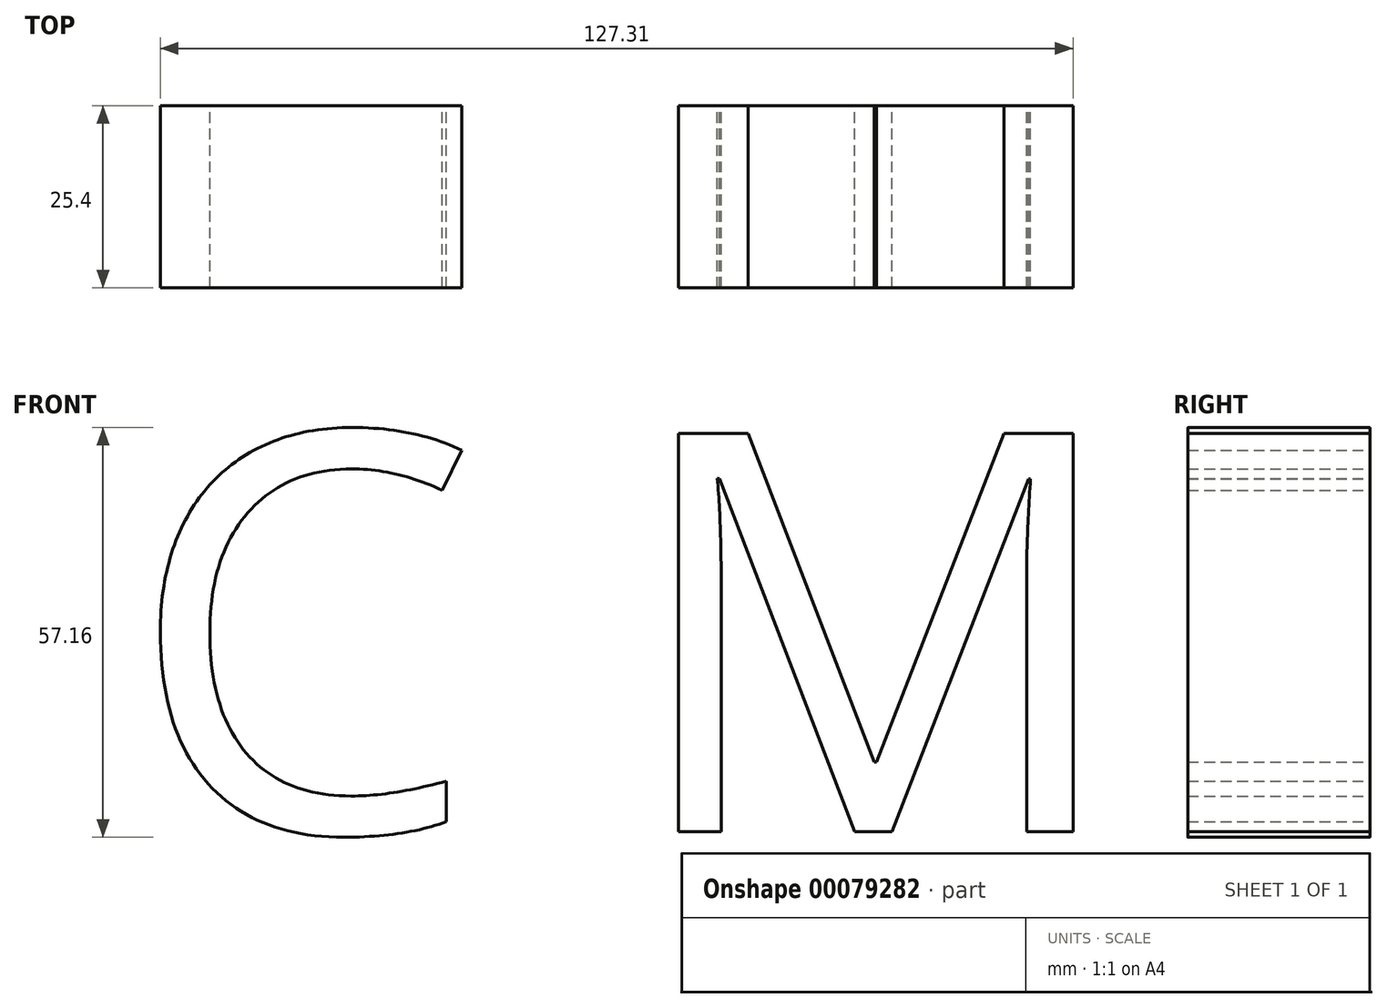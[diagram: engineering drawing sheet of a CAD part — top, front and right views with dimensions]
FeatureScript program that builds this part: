
annotation { "Feature Type Name" : "Feature", "Feature Type Description" : "" }
export const myFeature = defineFeature(function(context is Context, id is Id, definition is map)
    precondition{}
    {
        {
            var Q0;
            Q0=qCreatedBy(makeId("Front.planeOp"),FACE);
            var sketch = newSketch(context, id + "F0", { "sketchPlane" : qUnion([Q0])});
            skText(sketch, "E0", { "text": "C M", "fontName": "OpenSans-Regular.ttf"});
            const initialGuessF0  = {"E0": [0, 0, 1, 0, 0.05607]};
            skSetInitialGuess(sketch, initialGuessF0);
            skSolve(sketch);
        }
        {
            var Q0;
            Q0 = qSketchRegion(id + "F0", true);
            extrude(context, id + "F1", {"entities" : qUnion([Q0]), "depth" : 25.4 * mm});
        }
    });
